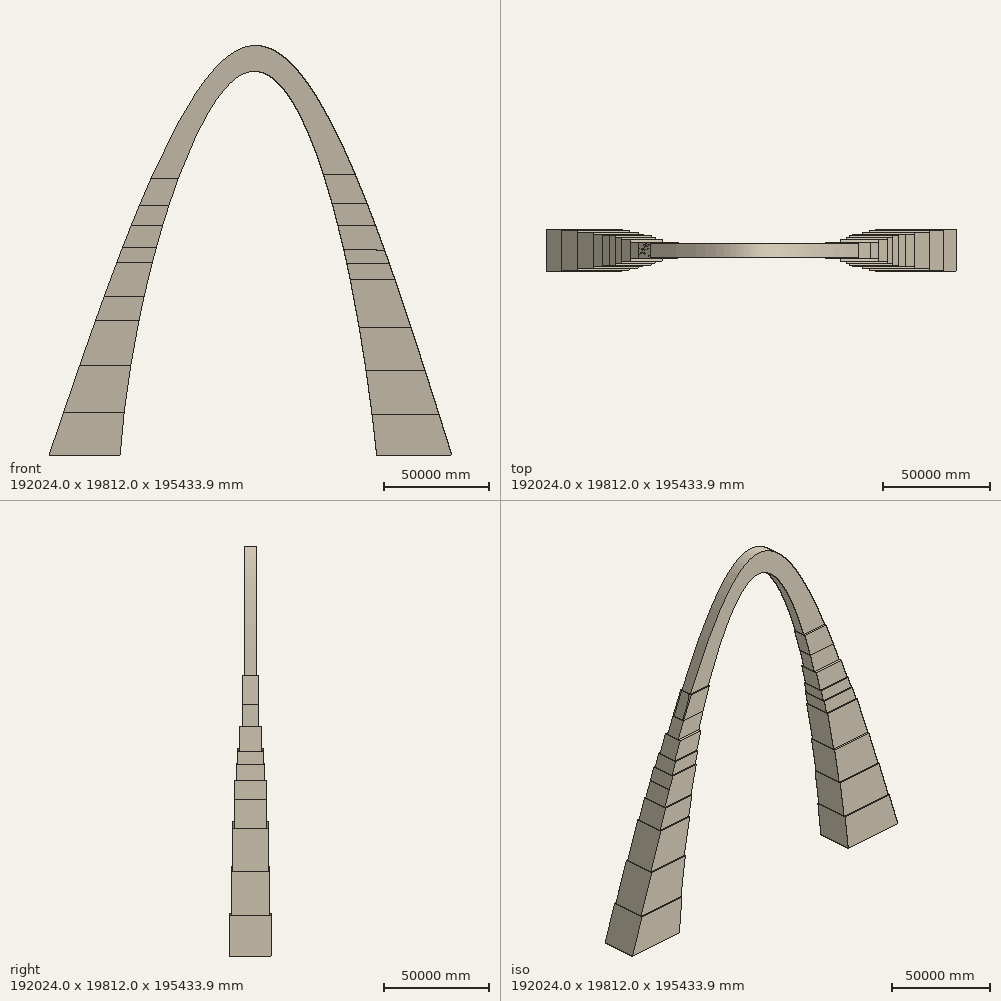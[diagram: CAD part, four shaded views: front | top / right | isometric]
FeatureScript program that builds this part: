
annotation { "Feature Type Name" : "Feature", "Feature Type Description" : "" }
export const myFeature = defineFeature(function(context is Context, id is Id, definition is map)
    precondition{}
    {
        {
            var Q0;
            Q0=qCreatedBy(makeId("Front.planeOp"),FACE);
            var sketch = newSketch(context, id + "F0", { "sketchPlane" : qUnion([Q0])});
            skLineSegment(sketch, "E0", {"start": v(235422.27, -7470.44) * mm, "end": v(235422.27, 184553.56) * mm});
            skLineSegment(sketch, "E1", {"start": v(222246.06, -9299.73) * mm, "end": v(30222.06, -9299.73) * mm});
            skFitSpline(sketch, "E2", {"points": [v(30222.06, -9299.73) * mm, v(128978.8, 186133.1) * mm, v(222246.06, -9299.73) * mm], "startDerivative": vector(199466.4, 588111.61) * mm, "endDerivative": vector(184950.9, -589079.56) * mm});
            skFitSpline(sketch, "E3", {"points": [v(64089.92, -9299.73) * mm, v(126863.14, 173704.32) * mm, v(186391.2, -9299.73) * mm], "startDerivative": vector(32282.43, 461807.5) * mm, "endDerivative": vector(56366.42, -546950.6) * mm});
            skLineSegment(sketch, "E4", {"start": v(178056.8, 51660.27) * mm, "end": v(202793.65, 51660.27) * mm});
            skLineSegment(sketch, "E5", {"start": v(73128.06, 55039.5) * mm, "end": v(52431.66, 55039.5) * mm});
            skLineSegment(sketch, "E6", {"start": v(185898.12, 100149.9) * mm, "end": v(167945.77, 100149.9) * mm});
            skLineSegment(sketch, "E7", {"start": v(84372.53, 100149.9) * mm, "end": v(69381.07, 100149.9) * mm});
            skLineSegment(sketch, "E8", {"start": v(81418.29, 89855.18) * mm, "end": v(65329.1, 89855.18) * mm});
            skLineSegment(sketch, "E9", {"start": v(62640.44, 82836.47) * mm, "end": v(79545.33, 82836.47) * mm});
            skLineSegment(sketch, "E10", {"start": v(59940.39, 75650.71) * mm, "end": v(77737.81, 75650.71) * mm});
            skLineSegment(sketch, "E11", {"start": v(79254.6, 75881.75) * mm, "end": v(75620.86, 66642.06) * mm});
            skLineSegment(sketch, "E12", {"start": v(56619.94, 66642.06) * mm, "end": v(75620.86, 66642.06) * mm});
            skLineSegment(sketch, "E13", {"start": v(87400.27, 109830.36) * mm, "end": v(73333.33, 109830.36) * mm});
            skLineSegment(sketch, "E14", {"start": v(165088.65, 110947.06) * mm, "end": v(181762.42, 110947.06) * mm});
            skLineSegment(sketch, "E15", {"start": v(170673.57, 88786.08) * mm, "end": v(191506.56, 88607.37) * mm});
            skLineSegment(sketch, "E16", {"start": v(190345.5, 90171.57) * mm, "end": v(192429.15, 82151.52) * mm});
            skLineSegment(sketch, "E17", {"start": v(192429.15, 82151.52) * mm, "end": v(172152.27, 82151.52) * mm});
            skLineSegment(sketch, "E18", {"start": v(172152.27, 82151.52) * mm, "end": v(173737.34, 74633) * mm});
            skLineSegment(sketch, "E19", {"start": v(173737.34, 74633) * mm, "end": v(195053, 74633) * mm});
            skLineSegment(sketch, "E20", {"start": v(195053, 74633) * mm, "end": v(198132.63, 65624.77) * mm});
            skLineSegment(sketch, "E21", {"start": v(198132.63, 65624.77) * mm, "end": v(177009.3, 65624.77) * mm});
            skLineSegment(sketch, "E22", {"start": v(44958.34, 33797.34) * mm, "end": v(69225.75, 33797.34) * mm});
            skLineSegment(sketch, "E23", {"start": v(181328.25, 31178.4) * mm, "end": v(209445.54, 31178.4) * mm});
            skLineSegment(sketch, "E24", {"start": v(37179.03, 11169.15) * mm, "end": v(66029.85, 11169.15) * mm});
            skLineSegment(sketch, "E25", {"start": v(184168.47, 10260.53) * mm, "end": v(216093.73, 10260.53) * mm});
            skLineSegment(sketch, "E26", {"start": v(78953.14, 122908.43) * mm, "end": v(91946.84, 122908.43) * mm});
            skLineSegment(sketch, "E27", {"start": v(161057.9, 124450.81) * mm, "end": v(176275.54, 124450.81) * mm});
            skSolve(sketch);
        }
        {
            var Q0;
            {var subQ0=sQuery(id+"F0.wireOp",EDGE,"E13");Q0=makeQuery(id+"F0.imprint","IMPRINT",FACE,{"disambiguationData":[TD([[makeQuery(id+"F0.imprint","IMPRINT",EDGE,{"derivedFrom":subQ0}),-1.0]])]});}
            extrude(context, id + "F1", {"entities" : qUnion([Q0]), "endBound" : BoundingType.SYMMETRIC, "depth" : 6096 * mm, "offsetDistance" : 30.48 * mm});
        }
        {
            var Q0;
            {var subQ0=sQuery(id+"F0.wireOp",EDGE,"E7");Q0=makeQuery(id+"F0.imprint","IMPRINT",FACE,{"disambiguationData":[TD([[makeQuery(id+"F0.imprint","IMPRINT",EDGE,{"derivedFrom":subQ0}),-1.0]])]});}
            var Q1;
            {var subQ0=sQuery(id+"F0.wireOp",EDGE,"E6");Q1=makeQuery(id+"F0.imprint","IMPRINT",FACE,{"disambiguationData":[TD([[makeQuery(id+"F0.imprint","IMPRINT",EDGE,{"derivedFrom":subQ0}),-1.0]])]});}
            extrude(context, id + "F2", {"entities" : qUnion([Q0, Q1]), "operationType" : NewBodyOperationType.ADD, "endBound" : BoundingType.SYMMETRIC, "depth" : 7620 * mm, "offsetDistance" : 30.48 * mm});
        }
        {
            var Q0;
            {var subQ0=sQuery(id+"F0.wireOp",EDGE,"E7");Q0=makeQuery(id+"F0.imprint","IMPRINT",FACE,{"disambiguationData":[TD([[makeQuery(id+"F0.imprint","IMPRINT",EDGE,{"derivedFrom":subQ0}),1.0]])]});}
            var Q1;
            {var subQ0=sQuery(id+"F0.wireOp",EDGE,"E6");Q1=makeQuery(id+"F0.imprint","IMPRINT",FACE,{"disambiguationData":[TD([[makeQuery(id+"F0.imprint","IMPRINT",EDGE,{"derivedFrom":subQ0}),1.0]])]});}
            extrude(context, id + "F3", {"entities" : qUnion([Q0, Q1]), "operationType" : NewBodyOperationType.ADD, "endBound" : BoundingType.SYMMETRIC, "depth" : 10668 * mm, "offsetDistance" : 30.48 * mm});
        }
        {
            var Q0;
            {var subQ0=sQuery(id+"F0.wireOp",EDGE,"E17");Q0=makeQuery(id+"F0.imprint","IMPRINT",FACE,{"disambiguationData":[TD([[makeQuery(id+"F0.imprint","IMPRINT",EDGE,{"derivedFrom":subQ0}),-1.0]])]});}
            var Q1;
            {var subQ0=sQuery(id+"F0.wireOp",EDGE,"E8");Q1=makeQuery(id+"F0.imprint","IMPRINT",FACE,{"disambiguationData":[TD([[makeQuery(id+"F0.imprint","IMPRINT",EDGE,{"derivedFrom":subQ0}),1.0]])]});}
            extrude(context, id + "F4", {"entities" : qUnion([Q0, Q1]), "operationType" : NewBodyOperationType.ADD, "endBound" : BoundingType.SYMMETRIC, "depth" : 12192 * mm, "offsetDistance" : 30.48 * mm});
        }
        {
            var Q0;
            {var subQ0=sQuery(id+"F0.wireOp",EDGE,"E9");Q0=makeQuery(id+"F0.imprint","IMPRINT",FACE,{"disambiguationData":[TD([[makeQuery(id+"F0.imprint","IMPRINT",EDGE,{"derivedFrom":subQ0}),-1.0]])]});}
            var Q1;
            {var subQ0=sQuery(id+"F0.wireOp",EDGE,"E17");Q1=makeQuery(id+"F0.imprint","IMPRINT",FACE,{"disambiguationData":[TD([[makeQuery(id+"F0.imprint","IMPRINT",EDGE,{"derivedFrom":subQ0}),1.0]])]});}
            extrude(context, id + "F5", {"entities" : qUnion([Q0, Q1]), "operationType" : NewBodyOperationType.ADD, "endBound" : BoundingType.SYMMETRIC, "depth" : 13716 * mm, "offsetDistance" : 30.48 * mm});
        }
        {
            var Q0;
            {var subQ0=sQuery(id+"F0.wireOp",EDGE,"E10");Q0=makeQuery(id+"F0.imprint","IMPRINT",FACE,{"disambiguationData":[TD([[makeQuery(id+"F0.imprint","IMPRINT",EDGE,{"derivedFrom":subQ0}),-1.0]])]});}
            var Q1;
            {var subQ0=sQuery(id+"F0.wireOp",EDGE,"E19");Q1=makeQuery(id+"F0.imprint","IMPRINT",FACE,{"disambiguationData":[TD([[makeQuery(id+"F0.imprint","IMPRINT",EDGE,{"derivedFrom":subQ0}),-1.0]])]});}
            extrude(context, id + "F6", {"entities" : qUnion([Q0, Q1]), "operationType" : NewBodyOperationType.ADD, "endBound" : BoundingType.SYMMETRIC, "depth" : 13716 * mm, "offsetDistance" : 30.48 * mm});
        }
        {
            var Q0;
            {var subQ0=sQuery(id+"F0.wireOp",EDGE,"E5");Q0=makeQuery(id+"F0.imprint","IMPRINT",FACE,{"disambiguationData":[TD([[makeQuery(id+"F0.imprint","IMPRINT",EDGE,{"derivedFrom":subQ0}),-1.0]])]});}
            var Q1;
            {var subQ0=sQuery(id+"F0.wireOp",EDGE,"E4");Q1=makeQuery(id+"F0.imprint","IMPRINT",FACE,{"disambiguationData":[TD([[makeQuery(id+"F0.imprint","IMPRINT",EDGE,{"derivedFrom":subQ0}),1.0]])]});}
            extrude(context, id + "F7", {"entities" : qUnion([Q0, Q1]), "operationType" : NewBodyOperationType.ADD, "endBound" : BoundingType.SYMMETRIC, "depth" : 15240 * mm, "offsetDistance" : 30.48 * mm});
        }
        {
            var Q0;
            {var subQ0=sQuery(id+"F0.wireOp",EDGE,"E5");Q0=makeQuery(id+"F0.imprint","IMPRINT",FACE,{"disambiguationData":[TD([[makeQuery(id+"F0.imprint","IMPRINT",EDGE,{"derivedFrom":subQ0}),1.0]])]});}
            var Q1;
            {var subQ0=sQuery(id+"F0.wireOp",EDGE,"E4");Q1=makeQuery(id+"F0.imprint","IMPRINT",FACE,{"disambiguationData":[TD([[makeQuery(id+"F0.imprint","IMPRINT",EDGE,{"derivedFrom":subQ0}),-1.0]])]});}
            extrude(context, id + "F8", {"entities" : qUnion([Q0, Q1]), "operationType" : NewBodyOperationType.ADD, "endBound" : BoundingType.SYMMETRIC, "depth" : 16764 * mm, "offsetDistance" : 30.48 * mm});
        }
        {
            var Q0;
            {var subQ0=sQuery(id+"F0.wireOp",EDGE,"E22");Q0=makeQuery(id+"F0.imprint","IMPRINT",FACE,{"disambiguationData":[TD([[makeQuery(id+"F0.imprint","IMPRINT",EDGE,{"derivedFrom":subQ0}),-1.0]])]});}
            var Q1;
            {var subQ0=sQuery(id+"F0.wireOp",EDGE,"E23");Q1=makeQuery(id+"F0.imprint","IMPRINT",FACE,{"disambiguationData":[TD([[makeQuery(id+"F0.imprint","IMPRINT",EDGE,{"derivedFrom":subQ0}),-1.0]])]});}
            extrude(context, id + "F9", {"entities" : qUnion([Q0, Q1]), "operationType" : NewBodyOperationType.ADD, "endBound" : BoundingType.SYMMETRIC, "depth" : 18288 * mm, "offsetDistance" : 30.48 * mm});
        }
        {
            var Q0;
            {var subQ5=sQuery(id+"F0.wireOp",EDGE,"E24");Q0=makeQuery(id+"F0.imprint","IMPRINT",FACE,{"disambiguationData":[TD([[makeQuery(id+"F0.imprint","IMPRINT",EDGE,{"derivedFrom":subQ5}),-1.0]])]});}
            var Q1;
            {var subQ5=sQuery(id+"F0.wireOp",EDGE,"E25");Q1=makeQuery(id+"F0.imprint","IMPRINT",FACE,{"disambiguationData":[TD([[makeQuery(id+"F0.imprint","IMPRINT",EDGE,{"derivedFrom":subQ5}),-1.0]])]});}
            extrude(context, id + "F10", {"entities" : qUnion([Q0, Q1]), "operationType" : NewBodyOperationType.ADD, "endBound" : BoundingType.SYMMETRIC, "depth" : 19812 * mm, "offsetDistance" : 30.48 * mm});
        }
        {
            var Q0;
            {var subQ0=sQuery(id+"F0.wireOp",EDGE,"E13");Q0=makeQuery(id+"F0.imprint","IMPRINT",FACE,{"disambiguationData":[TD([[makeQuery(id+"F0.imprint","IMPRINT",EDGE,{"derivedFrom":subQ0}),-1.0]])]});}
            var Q1;
            {var subQ0=sQuery(id+"F0.wireOp",EDGE,"E14");Q1=makeQuery(id+"F0.imprint","IMPRINT",FACE,{"disambiguationData":[TD([[makeQuery(id+"F0.imprint","IMPRINT",EDGE,{"derivedFrom":subQ0}),1.0]])]});}
            extrude(context, id + "F11", {"entities" : qUnion([Q0, Q1]), "endBound" : BoundingType.SYMMETRIC, "depth" : 7620 * mm, "offsetDistance" : 30.48 * mm});
        }
        {
            var Q0;
            {var subQ0=sQuery(id+"F0.wireOp",EDGE,"E26");Q0=makeQuery(id+"F0.imprint","IMPRINT",FACE,{"disambiguationData":[TD([[makeQuery(id+"F0.imprint","IMPRINT",EDGE,{"derivedFrom":subQ0}),1.0]])]});}
            extrude(context, id + "F12", {"entities" : qUnion([Q0]), "endBound" : BoundingType.SYMMETRIC, "depth" : 6096 * mm, "offsetDistance" : 30.48 * mm});
        }
    });
